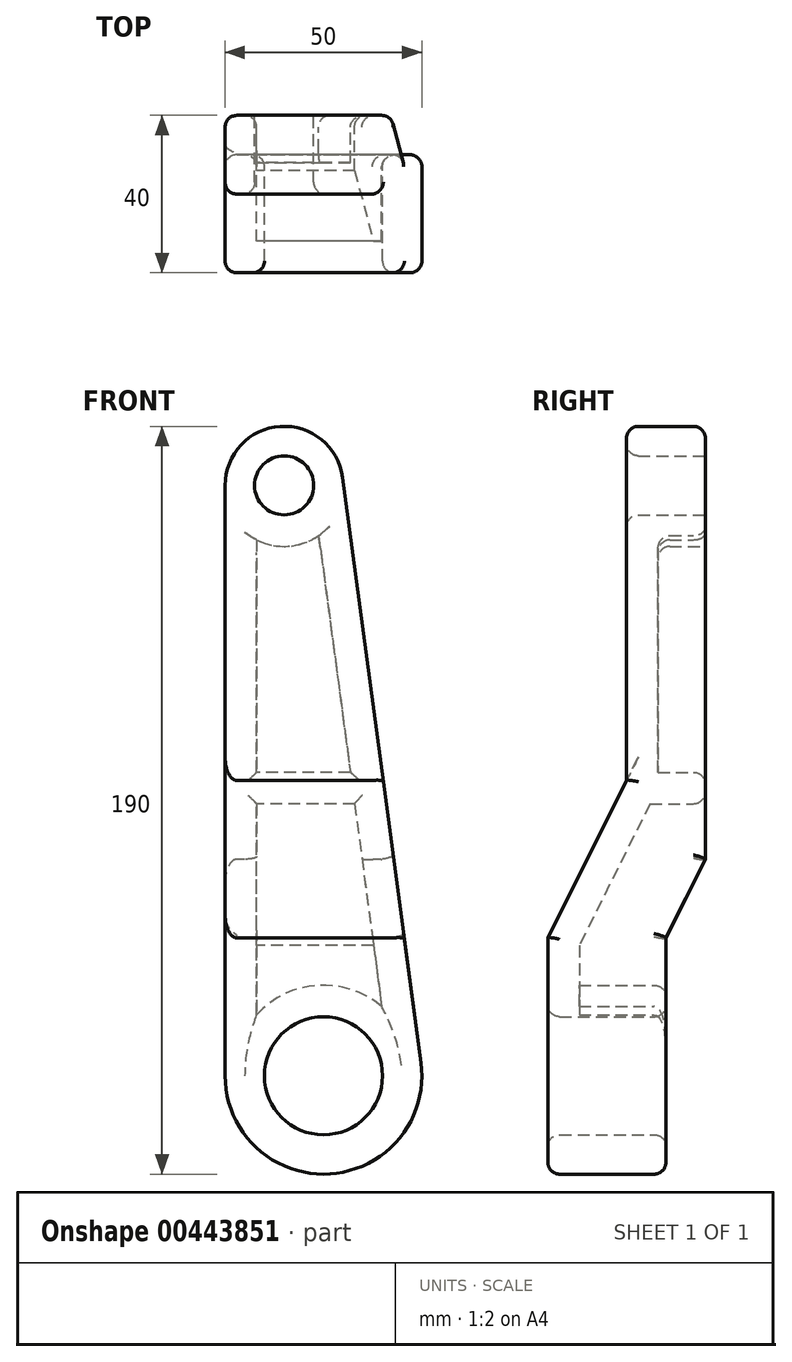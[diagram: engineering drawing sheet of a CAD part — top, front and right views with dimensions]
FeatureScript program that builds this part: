
annotation { "Feature Type Name" : "Feature", "Feature Type Description" : "" }
export const myFeature = defineFeature(function(context is Context, id is Id, definition is map)
    precondition{}
    {
        {
            var Q0;
            Q0=qCreatedBy(makeId("Front.planeOp"),FACE);
            var sketch = newSketch(context, id + "F0", { "sketchPlane" : qUnion([Q0])});
            skCircle(sketch, "E0", {"center": v(0, 0) * mm, "radius": 25 * mm});
            skCircle(sketch, "E1", {"center": v(-10, 150) * mm, "radius": 15 * mm});
            skLineSegment(sketch, "E2", {"start": v(-25, 150) * mm, "end": v(-25, 0) * mm});
            skLineSegment(sketch, "E3", {"start": v(4.87, 152) * mm, "end": v(24.78, 3.32) * mm});
            skSolve(sketch);
        }
        {
            var Q0;
            Q0 = qSketchRegion(id + "F0", true);
            extrude(context, id + "F1", {"entities" : qUnion([Q0]), "depth" : 40 * mm});
        }
        {
            var Q0;
            Q0=makeQuery(id+"F1.opExtrude","SWEPT_FACE",FACE,{"disambiguationData":[OSD([sQuery(id+"F0.wireOp",EDGE,"E2")])]});
            var sketch = newSketch(context, id + "F2", { "sketchPlane" : qUnion([Q0])});
            skLineSegment(sketch, "E4", {"start": v(0, 0) * mm, "end": v(0, -25.94) * mm});
            skLineSegment(sketch, "E5", {"start": v(10, -25.94) * mm, "end": v(10, 35) * mm});
            skLineSegment(sketch, "E6", {"start": v(10, 35) * mm, "end": v(0, 55) * mm});
            skLineSegment(sketch, "E7", {"start": v(0, 55) * mm, "end": v(0, 0) * mm});
            skLineSegment(sketch, "E8", {"start": v(40, 165.97) * mm, "end": v(40, 35) * mm});
            skLineSegment(sketch, "E9", {"start": v(40, 35) * mm, "end": v(20, 75) * mm});
            skLineSegment(sketch, "E10", {"start": v(20, 75) * mm, "end": v(20, 165.97) * mm});
            skLineSegment(sketch, "E11", {"start": v(10, -25.94) * mm, "end": v(0, -25.94) * mm});
            skLineSegment(sketch, "E12", {"start": v(20, 165.97) * mm, "end": v(40, 165.97) * mm});
            skSolve(sketch);
        }
        {
            var Q0;
            Q0 = qSketchRegion(id + "F2", true);
            extrude(context, id + "F3", {"entities" : qUnion([Q0]), "operationType" : NewBodyOperationType.REMOVE, "endBound" : BoundingType.THROUGH_ALL, "oppositeDirection" : true, "depth" : 25 * mm});
        }
        {
            var Q0;
            Q0=makeQuery(id+"F1.opExtrude","CAP_FACE",FACE,{"disambiguationData":[OSD([sQuery(id+"F0.wireOp",EDGE,"E0"),sQuery(id+"F0.wireOp",EDGE,"E1"),sQuery(id+"F0.wireOp",EDGE,"E2"),sQuery(id+"F0.wireOp",EDGE,"E3")])],"isStart":true});
            var sketch = newSketch(context, id + "F4", { "sketchPlane" : qUnion([Q0])});
            skCircle(sketch, "E13", {"center": v(10, 150) * mm, "radius": 7.5 * mm});
            skCircle(sketch, "E14", {"center": v(0, 0) * mm, "radius": 15 * mm});
            skSolve(sketch);
        }
        {
            var Q0;
            Q0=makeQuery(id+"F4.imprint","IMPRINT",FACE,{"disambiguationData":[TD([[makeQuery(id+"F4.imprint","IMPRINT",EDGE,{"derivedFrom":sQuery(id+"F4.wireOp",EDGE,"E13")}),1.0]])]});
            var Q1;
            Q1=makeQuery(id+"F4.imprint","IMPRINT",FACE,{"disambiguationData":[TD([[makeQuery(id+"F4.imprint","IMPRINT",EDGE,{"derivedFrom":sQuery(id+"F4.wireOp",EDGE,"E14")}),1.0]])]});
            extrude(context, id + "F5", {"entities" : qUnion([Q0, Q1]), "operationType" : NewBodyOperationType.REMOVE, "endBound" : BoundingType.THROUGH_ALL, "oppositeDirection" : true, "depth" : 25 * mm});
        }
        {
            var Q0;
            Q0=makeQuery(id+"F1.opExtrude","CAP_FACE",FACE,{"disambiguationData":[OSD([sQuery(id+"F0.wireOp",EDGE,"E0"),sQuery(id+"F0.wireOp",EDGE,"E1"),sQuery(id+"F0.wireOp",EDGE,"E2"),sQuery(id+"F0.wireOp",EDGE,"E3")])],"isStart":true});
            var Q1;
            Q1=makeQuery(id+"F3.boolean.opBoolean","COPY",FACE,{"derivedFrom":makeQuery(id+"F3.opExtrude","SWEPT_FACE",FACE,{"disambiguationData":[OSD([sQuery(id+"F2.wireOp",EDGE,"E6")])]})});
            var Q2;
            Q2=makeQuery(id+"F3.boolean.opBoolean","COPY",FACE,{"derivedFrom":makeQuery(id+"F3.opExtrude","SWEPT_FACE",FACE,{"disambiguationData":[OSD([sQuery(id+"F2.wireOp",EDGE,"E5")])]})});
            shell(context, id + "F6", {"entities" : qUnion([Q0, Q1, Q2]), "thickness" : 8 * mm});
        }
        {
            var Q0;
            Q0=makeQuery(id+"F1.opExtrude","CAP_FACE",FACE,{"disambiguationData":[OSD([sQuery(id+"F0.wireOp",EDGE,"E0"),sQuery(id+"F0.wireOp",EDGE,"E1"),sQuery(id+"F0.wireOp",EDGE,"E2"),sQuery(id+"F0.wireOp",EDGE,"E3")])],"isStart":true});
            var sketch = newSketch(context, id + "F7", { "sketchPlane" : qUnion([Q0])});
            skLineSegment(sketch, "E15", {"start": v(-6.82, 77.11) * mm, "end": v(17, 77.11) * mm});
            skLineSegment(sketch, "E16", {"start": v(-7.9, 69.11) * mm, "end": v(17, 69.11) * mm});
            skLineSegment(sketch, "E17.0", {"start": v(1.23, 137.22) * mm, "end": v(-9.79, 55) * mm});
            skLineSegment(sketch, "E18.0", {"start": v(17, 136.17) * mm, "end": v(17, 55) * mm});
            skSolve(sketch);
        }
        {
            var Q0;
            Q0 = qSketchRegion(id + "F7", true);
            extrude(context, id + "F8", {"entities" : qUnion([Q0]), "operationType" : NewBodyOperationType.ADD, "endBound" : BoundingType.UP_TO_NEXT, "oppositeDirection" : true, "depth" : 25 * mm});
        }
        {
            var Q0;
            Q0=makeQuery(id+"F3.boolean.opBoolean","INTERSECT",EDGE,{"derivedFrom":[makeQuery(id+"F1.opExtrude","SWEPT_FACE",FACE,{"disambiguationData":[OSD([sQuery(id+"F0.wireOp",EDGE,"E3")])]}),makeQuery(id+"F3.opExtrude","SWEPT_FACE",FACE,{"disambiguationData":[OSD([sQuery(id+"F2.wireOp",EDGE,"E10")])]})]});
            var Q1;
            Q1=makeQuery(id+"F1.opExtrude","CAP_EDGE",EDGE,{"disambiguationData":[OSD([sQuery(id+"F0.wireOp",EDGE,"E3")])],"isStart":true});
            var Q2;
            Q2=makeQuery(id+"F1.opExtrude","CAP_EDGE",EDGE,{"disambiguationData":[OSD([sQuery(id+"F0.wireOp",EDGE,"E1")])],"isStart":true});
            var Q3;
            Q3=makeQuery(id+"F1.opExtrude","CAP_EDGE",EDGE,{"disambiguationData":[OSD([sQuery(id+"F0.wireOp",EDGE,"E2")])],"isStart":true});
            var Q4;
            Q4=makeQuery(id+"F5.boolean.opBoolean","COPY",EDGE,{"derivedFrom":makeQuery(id+"F5.opExtrude","CAP_EDGE",EDGE,{"disambiguationData":[OSD([sQuery(id+"F4.wireOp",EDGE,"E13")])],"isStart":true})});
            var Q5;
            {var subQ1=sQuery(id+"F0.wireOp",EDGE,"E2");Q5=makeQuery(id+"F8.boolean.opBoolean","SPLIT",EDGE,{"disambiguationData":[TD([makeQuery(id+"F6.opShell","OFFSET_FACE",FACE,{"disambiguationData":[OSD([sQuery(id+"F4.wireOp",EDGE,"E13")])]})])],"derivedFrom":makeQuery(id+"F6.opShell","OFFSET_EDGE",EDGE,{"disambiguationData":[OSD([subQ1]),TDD([makeQuery(id+"F1.opExtrude","CAP_EDGE",EDGE,{"disambiguationData":[OSD([subQ1])],"isStart":true})])]})});}
            var Q6;
            Q6=makeQuery(id+"F6.opShell","OFFSET_EDGE",EDGE,{"disambiguationData":[OSD([sQuery(id+"F4.wireOp",EDGE,"E13")])]});
            var Q7;
            {var subQ1=sQuery(id+"F0.wireOp",EDGE,"E3");Q7=makeQuery(id+"F8.boolean.opBoolean","SPLIT",EDGE,{"disambiguationData":[TD([makeQuery(id+"F6.opShell","OFFSET_FACE",FACE,{"disambiguationData":[OSD([sQuery(id+"F4.wireOp",EDGE,"E13")])]})])],"derivedFrom":makeQuery(id+"F6.opShell","OFFSET_EDGE",EDGE,{"disambiguationData":[OSD([subQ1]),TDD([makeQuery(id+"F1.opExtrude","CAP_EDGE",EDGE,{"disambiguationData":[OSD([subQ1])],"isStart":true})])]})});}
            var Q8;
            Q8=makeQuery(id+"F8.opExtrude","CAP_EDGE",EDGE,{"disambiguationData":[OSD([sQuery(id+"F7.wireOp",EDGE,"E15")])],"isStart":true});
            var Q9;
            {var subQ1=sQuery(id+"F0.wireOp",EDGE,"E3");Q9=makeQuery(id+"F8.boolean.opBoolean","SPLIT",EDGE,{"disambiguationData":[TD([makeQuery(id+"F6.opShell","OFFSET_FACE",FACE,{"disambiguationData":[OSD([sQuery(id+"F2.wireOp",EDGE,"E6")])]})])],"derivedFrom":makeQuery(id+"F6.opShell","OFFSET_EDGE",EDGE,{"disambiguationData":[OSD([subQ1]),TDD([makeQuery(id+"F1.opExtrude","CAP_EDGE",EDGE,{"disambiguationData":[OSD([subQ1])],"isStart":true})])]})});}
            var Q10;
            Q10=makeQuery(id+"F8.opExtrude","CAP_EDGE",EDGE,{"disambiguationData":[OSD([sQuery(id+"F7.wireOp",EDGE,"E16")])],"isStart":true});
            var Q11;
            {var subQ0=sQuery(id+"F0.wireOp",EDGE,"E2");Q11=makeQuery(id+"F8.boolean.opBoolean","SPLIT",EDGE,{"disambiguationData":[TD([makeQuery(id+"F3.boolean.opBoolean","COPY",FACE,{"derivedFrom":makeQuery(id+"F3.opExtrude","SWEPT_FACE",FACE,{"disambiguationData":[OSD([sQuery(id+"F2.wireOp",EDGE,"E6")])]})})])],"derivedFrom":makeQuery(id+"F6.opShell","OFFSET_EDGE",EDGE,{"disambiguationData":[OSD([subQ0]),TDD([makeQuery(id+"F1.opExtrude","CAP_EDGE",EDGE,{"disambiguationData":[OSD([subQ0])],"isStart":true})])]})});}
            var Q12;
            Q12=makeQuery(id+"F6.opShell","OFFSET_EDGE",EDGE,{"disambiguationData":[OSD([sQuery(id+"F2.wireOp",EDGE,"E6")])]});
            var Q13;
            Q13=makeQuery(id+"F3.boolean.opBoolean","COPY",EDGE,{"derivedFrom":makeQuery(id+"F3.opExtrude","CAP_EDGE",EDGE,{"disambiguationData":[OSD([sQuery(id+"F2.wireOp",EDGE,"E6")])],"isStart":true})});
            var Q14;
            Q14=makeQuery(id+"F3.boolean.opBoolean","COPY",EDGE,{"derivedFrom":makeQuery(id+"F3.opExtrude","CAP_EDGE",EDGE,{"disambiguationData":[OSD([sQuery(id+"F2.wireOp",EDGE,"E5")])],"isStart":true})});
            var Q15;
            Q15=makeQuery(id+"F6.opShell","OFFSET_EDGE",EDGE,{"disambiguationData":[OSD([sQuery(id+"F2.wireOp",EDGE,"E5")])]});
            var Q16;
            Q16=makeQuery(id+"F6.opShell","OFFSET_EDGE",EDGE,{"disambiguationData":[OSD([sQuery(id+"F2.wireOp",EDGE,"E5"),sQuery(id+"F4.wireOp",EDGE,"E14")])]});
            var Q17;
            Q17=makeQuery(id+"F6.opShell","OFFSET_EDGE",EDGE,{"disambiguationData":[OSD([sQuery(id+"F0.wireOp",EDGE,"E3"),sQuery(id+"F2.wireOp",EDGE,"E5")])]});
            var Q18;
            Q18=makeQuery(id+"F6.opShell","OFFSET_EDGE",EDGE,{"disambiguationData":[OSD([sQuery(id+"F0.wireOp",EDGE,"E3"),sQuery(id+"F2.wireOp",EDGE,"E6")])]});
            var Q19;
            Q19=makeQuery(id+"F3.boolean.opBoolean","INTERSECT",EDGE,{"derivedFrom":[makeQuery(id+"F1.opExtrude","SWEPT_FACE",FACE,{"disambiguationData":[OSD([sQuery(id+"F0.wireOp",EDGE,"E3")])]}),makeQuery(id+"F3.opExtrude","SWEPT_FACE",FACE,{"disambiguationData":[OSD([sQuery(id+"F2.wireOp",EDGE,"E6")])]})]});
            var Q20;
            Q20=makeQuery(id+"F3.boolean.opBoolean","INTERSECT",EDGE,{"derivedFrom":[makeQuery(id+"F1.opExtrude","SWEPT_FACE",FACE,{"disambiguationData":[OSD([sQuery(id+"F0.wireOp",EDGE,"E3")])]}),makeQuery(id+"F3.opExtrude","SWEPT_FACE",FACE,{"disambiguationData":[OSD([sQuery(id+"F2.wireOp",EDGE,"E5")])]})]});
            var Q21;
            Q21=makeQuery(id+"F5.boolean.opBoolean","INTERSECT",EDGE,{"derivedFrom":[makeQuery(id+"F3.boolean.opBoolean","COPY",FACE,{"derivedFrom":makeQuery(id+"F3.opExtrude","SWEPT_FACE",FACE,{"disambiguationData":[OSD([sQuery(id+"F2.wireOp",EDGE,"E5")])]})}),makeQuery(id+"F5.opExtrude","SWEPT_FACE",FACE,{"disambiguationData":[OSD([sQuery(id+"F4.wireOp",EDGE,"E14")])]})]});
            var Q22;
            Q22=makeQuery(id+"F3.boolean.opBoolean","INTERSECT",EDGE,{"derivedFrom":[makeQuery(id+"F1.opExtrude","SWEPT_FACE",FACE,{"disambiguationData":[OSD([sQuery(id+"F0.wireOp",EDGE,"E0")])]}),makeQuery(id+"F3.opExtrude","SWEPT_FACE",FACE,{"disambiguationData":[OSD([sQuery(id+"F2.wireOp",EDGE,"E5")])]})]});
            var Q23;
            Q23=makeQuery(id+"F3.boolean.opBoolean","INTERSECT",EDGE,{"derivedFrom":[makeQuery(id+"F1.opExtrude","SWEPT_FACE",FACE,{"disambiguationData":[OSD([sQuery(id+"F0.wireOp",EDGE,"E3")])]}),makeQuery(id+"F3.opExtrude","SWEPT_FACE",FACE,{"disambiguationData":[OSD([sQuery(id+"F2.wireOp",EDGE,"E9")])]})]});
            var Q24;
            Q24=makeQuery(id+"F1.opExtrude","CAP_EDGE",EDGE,{"disambiguationData":[OSD([sQuery(id+"F0.wireOp",EDGE,"E3")])],"isStart":false});
            var Q25;
            Q25=makeQuery(id+"F1.opExtrude","CAP_EDGE",EDGE,{"disambiguationData":[OSD([sQuery(id+"F0.wireOp",EDGE,"E0")])],"isStart":false});
            var Q26;
            Q26=makeQuery(id+"F5.boolean.opBoolean","INTERSECT",EDGE,{"derivedFrom":[makeQuery(id+"F1.opExtrude","CAP_FACE",FACE,{"disambiguationData":[OSD([sQuery(id+"F0.wireOp",EDGE,"E0"),sQuery(id+"F0.wireOp",EDGE,"E1"),sQuery(id+"F0.wireOp",EDGE,"E2"),sQuery(id+"F0.wireOp",EDGE,"E3")])],"isStart":false}),makeQuery(id+"F5.opExtrude","SWEPT_FACE",FACE,{"disambiguationData":[OSD([sQuery(id+"F4.wireOp",EDGE,"E14")])]})]});
            var Q27;
            Q27=makeQuery(id+"F1.opExtrude","CAP_EDGE",EDGE,{"disambiguationData":[OSD([sQuery(id+"F0.wireOp",EDGE,"E2")])],"isStart":false});
            var Q28;
            Q28=makeQuery(id+"F3.boolean.opBoolean","COPY",EDGE,{"derivedFrom":makeQuery(id+"F3.opExtrude","CAP_EDGE",EDGE,{"disambiguationData":[OSD([sQuery(id+"F2.wireOp",EDGE,"E9")])],"isStart":true})});
            var Q29;
            Q29=makeQuery(id+"F3.boolean.opBoolean","COPY",EDGE,{"derivedFrom":makeQuery(id+"F3.opExtrude","CAP_EDGE",EDGE,{"disambiguationData":[OSD([sQuery(id+"F2.wireOp",EDGE,"E10")])],"isStart":true})});
            var Q30;
            Q30=makeQuery(id+"F3.boolean.opBoolean","INTERSECT",EDGE,{"derivedFrom":[makeQuery(id+"F1.opExtrude","SWEPT_FACE",FACE,{"disambiguationData":[OSD([sQuery(id+"F0.wireOp",EDGE,"E1")])]}),makeQuery(id+"F3.opExtrude","SWEPT_FACE",FACE,{"disambiguationData":[OSD([sQuery(id+"F2.wireOp",EDGE,"E10")])]})]});
            var Q31;
            Q31=makeQuery(id+"F5.boolean.opBoolean","INTERSECT",EDGE,{"derivedFrom":[makeQuery(id+"F3.boolean.opBoolean","COPY",FACE,{"derivedFrom":makeQuery(id+"F3.opExtrude","SWEPT_FACE",FACE,{"disambiguationData":[OSD([sQuery(id+"F2.wireOp",EDGE,"E10")])]})}),makeQuery(id+"F5.opExtrude","SWEPT_FACE",FACE,{"disambiguationData":[OSD([sQuery(id+"F4.wireOp",EDGE,"E13")])]})]});
            fillet(context, id + "F9", {"entities" : qUnion([Q0, Q1, Q2, Q3, Q4, Q5, Q6, Q7, Q8, Q9, Q10, Q11, Q12, Q13, Q14, Q15, Q16, Q17, Q18, Q19, Q20, Q21, Q22, Q23, Q24, Q25, Q26, Q27, Q28, Q29, Q30, Q31]), "radius" : 3 * mm, "tangentPropagation" : true, "allowEdgeOverflow" : false});
        }
    });
